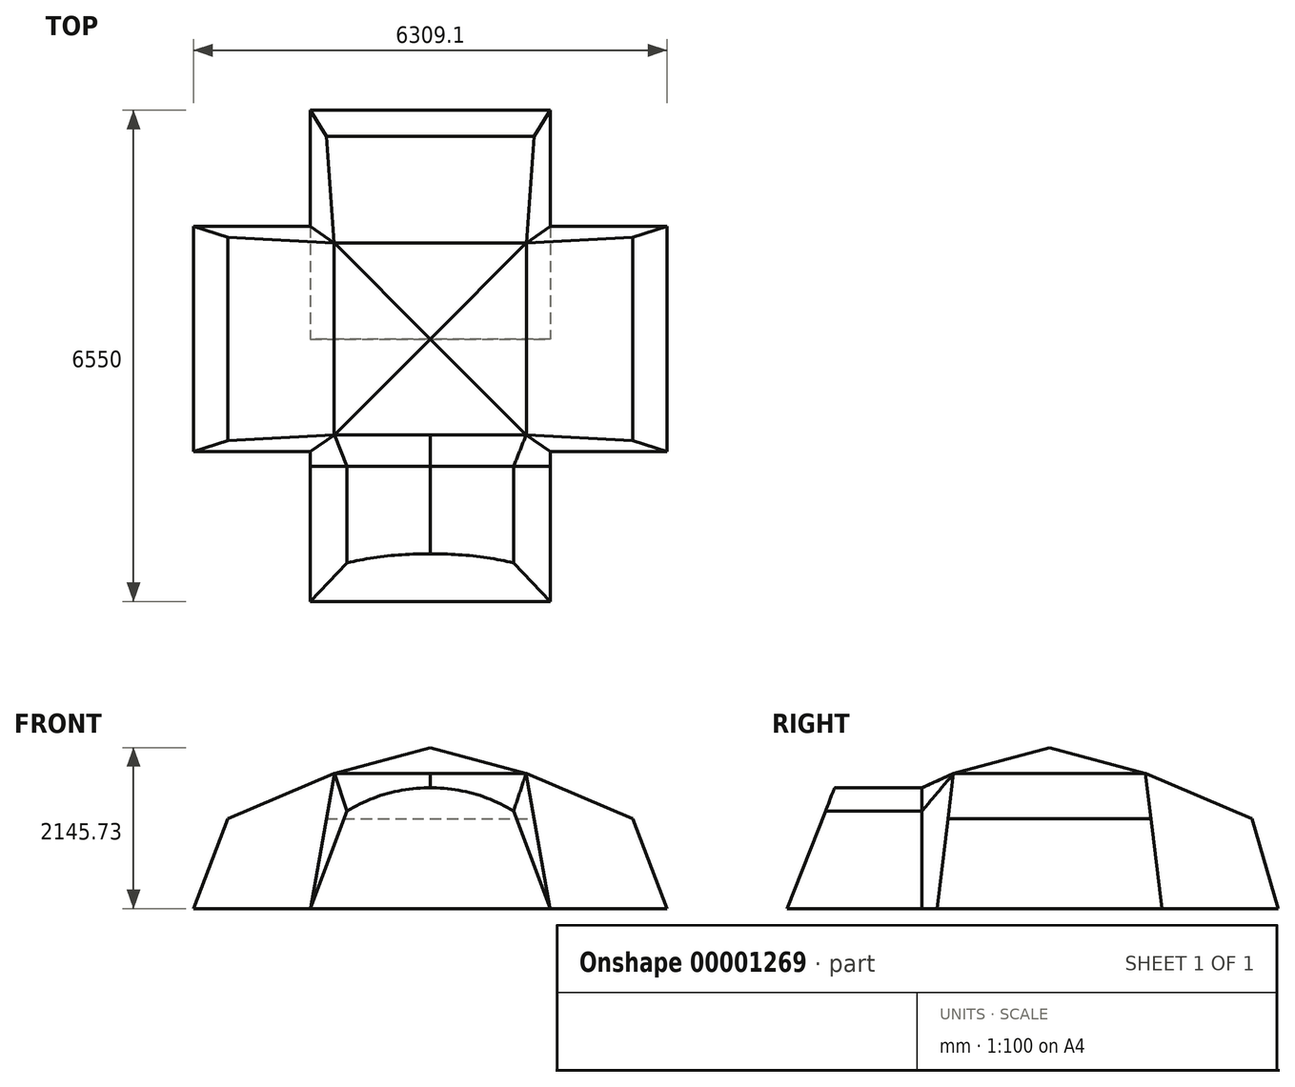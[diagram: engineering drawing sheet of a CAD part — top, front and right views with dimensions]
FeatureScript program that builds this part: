
annotation { "Feature Type Name" : "Feature", "Feature Type Description" : "" }
export const myFeature = defineFeature(function(context is Context, id is Id, definition is map)
    precondition{}
    {
        {
            var Q0;
            Q0=qCreatedBy(makeId("Top.planeOp"),FACE);
            var sketch = newSketch(context, id + "F0", { "sketchPlane" : qUnion([Q0])});
            skLineSegment(sketch, "E0.rect.bottom", {"start": v(0, -1500) * mm, "end": v(-1600, -1500) * mm, "construction": true});
            skLineSegment(sketch, "E0.rect.top", {"start": v(0, 1500) * mm, "end": v(-1600, 1500) * mm, "construction": true});
            skLineSegment(sketch, "E0.rect.right", {"start": v(-1600, -1500) * mm, "end": v(-1600, 1500) * mm, "construction": true});
            skPoint(sketch, "E0.rect.middle", {"position": v(0, 0) * mm});
            skLineSegment(sketch, "E1.bottom", {"start": v(-1600, -1500) * mm, "end": v(-3150, -1500) * mm});
            skLineSegment(sketch, "E1.top", {"start": v(-1600, 1500) * mm, "end": v(-3150, 1500) * mm});
            skLineSegment(sketch, "E1.right", {"start": v(-3150, -1500) * mm, "end": v(-3150, 1500) * mm});
            skLineSegment(sketch, "E2.top", {"start": v(-1600, -3500) * mm, "end": v(0, -3500) * mm});
            skLineSegment(sketch, "E2.left", {"start": v(-1600, -1500) * mm, "end": v(-1600, -3500) * mm});
            skLineSegment(sketch, "E3.top", {"start": v(0, 3050) * mm, "end": v(-1600, 3050) * mm});
            skLineSegment(sketch, "E3.right", {"start": v(-1600, 1500) * mm, "end": v(-1600, 3050) * mm});
            skLineSegment(sketch, "E4", {"start": v(0, 3050) * mm, "end": v(0, -3500) * mm});
            skLineSegment(sketch, "E5", {"start": v(0, 0) * mm, "end": v(-3150, 0) * mm, "construction": true});
            skSolve(sketch);
        }
        {
            var Q0;
            Q0=qCreatedBy(makeId("Front.planeOp"),FACE);
            var sketch = newSketch(context, id + "F1", { "sketchPlane" : qUnion([Q0])});
            skArc(sketch, "E6", {"start": v(0, 1610) * mm, "mid": v(-576.9, 1533.43) * mm, "end": v(-1110, 1300) * mm});
            skPoint(sketch, "E7.rect.middle", {"position": v(0, 0) * mm});
            skLineSegment(sketch, "E8", {"start": v(0, 2145.46) * mm, "end": v(0, 0) * mm});
            skLineSegment(sketch, "E9", {"start": v(-1280, 1799.46) * mm, "end": v(0, 2145.46) * mm});
            skLineSegment(sketch, "E10", {"start": v(-1600, -0.27) * mm, "end": v(-1600, 2068.8) * mm, "construction": true});
            skLineSegment(sketch, "E11", {"start": v(-3154.76, -0.54) * mm, "end": v(-2700, 1199.46) * mm});
            skPoint(sketch, "E12", {"position": v(-2700, 1199.46) * mm});
            skLineSegment(sketch, "E13", {"start": v(-1280, 1799.46) * mm, "end": v(-2700, 1199.46) * mm});
            skLineSegment(sketch, "E14", {"start": v(-1600, -0.27) * mm, "end": v(-1280, 1799.46) * mm});
            skLineSegment(sketch, "E15", {"start": v(-1280, 1799.46) * mm, "end": v(0, 1799.46) * mm});
            skLineSegment(sketch, "E16", {"start": v(0, 1799.46) * mm, "end": v(0, 1610) * mm});
            skLineSegment(sketch, "E17", {"start": v(-1600, -0.27) * mm, "end": v(-1110, 1300) * mm});
            skLineSegment(sketch, "E18", {"start": v(-3154.76, -0.54) * mm, "end": v(0, 0) * mm});
            skSolve(sketch);
        }
        {
            var Q0;
            Q0=qCreatedBy(makeId("Right.planeOp"),FACE);
            var sketch = newSketch(context, id + "F2", { "sketchPlane" : qUnion([Q0])});
            skLineSegment(sketch, "E19", {"start": v(-1500, 0) * mm, "end": v(1500, 0) * mm});
            skLineSegment(sketch, "E20", {"start": v(-3500, 0) * mm, "end": v(0, 0) * mm});
            skLineSegment(sketch, "E21", {"start": v(0, 0) * mm, "end": v(0, 1800) * mm});
            skLineSegment(sketch, "E22.MirrorCS", {"start": v(3050, 0) * mm, "end": v(2701.24, 1200) * mm});
            skLineSegment(sketch, "E23.MirrorCS", {"start": v(1280, 1800) * mm, "end": v(2701.24, 1200) * mm});
            skLineSegment(sketch, "E24", {"start": v(1280, 1800) * mm, "end": v(0, 2145.46) * mm});
            skLineSegment(sketch, "E25", {"start": v(1500, 0) * mm, "end": v(3050, 0) * mm});
            skLineSegment(sketch, "E26", {"start": v(1500, 0) * mm, "end": v(1280, 1800) * mm});
            skLineSegment(sketch, "E27", {"start": v(0, 1800) * mm, "end": v(1280, 1800) * mm});
            skLineSegment(sketch, "E28.MirrorCS", {"start": v(0, 1800) * mm, "end": v(-1280, 1800) * mm});
            skLineSegment(sketch, "E29", {"start": v(-1500, 0) * mm, "end": v(-1280, 1800) * mm});
            skLineSegment(sketch, "E30", {"start": v(0, 2145.46) * mm, "end": v(-1280, 1800) * mm});
            skLineSegment(sketch, "E31", {"start": v(1280, 1800) * mm, "end": v(3050, 1800) * mm});
            skLineSegment(sketch, "E32", {"start": v(3050, 0) * mm, "end": v(3050, 1800) * mm});
            skSolve(sketch);
        }
        {
            var Q0;
            {var subQ0=sQuery(id+"F1.wireOp",EDGE,"E9");Q0=makeQuery(id+"F1.imprint","IMPRINT",FACE,{"disambiguationData":[TD([[makeQuery(id+"F1.imprint","IMPRINT",EDGE,{"derivedFrom":subQ0}),-1.0]])]});}
            var Q1;
            {var subQ1=sQuery(id+"F1.wireOp",EDGE,"E6");Q1=makeQuery(id+"F1.imprint","IMPRINT",FACE,{"disambiguationData":[TD([[makeQuery(id+"F1.imprint","IMPRINT",EDGE,{"derivedFrom":subQ1}),-1.0]])]});}
            var Q2;
            {var subQ0=sQuery(id+"F1.wireOp",EDGE,"E6");Q2=makeQuery(id+"F1.imprint","IMPRINT",FACE,{"disambiguationData":[TD([[makeQuery(id+"F1.imprint","IMPRINT",EDGE,{"derivedFrom":subQ0}),1.0]])]});}
            var Q3;
            Q3=makeQuery(id+"F1.imprint","IMPRINT",FACE,{"disambiguationData":[TD([[makeQuery(id+"F1.imprint","IMPRINT",EDGE,{"derivedFrom":sQuery(id+"F1.wireOp",EDGE,"E11")}),-1.0]])]});
            extrude(context, id + "F3", {"entities" : qUnion([Q0, Q1, Q2, Q3]), "depth" : 3000 * mm, "symmetric" : true});
        }
        {
            var Q0;
            Q0=makeQuery(id+"F2.imprint","IMPRINT",FACE,{"disambiguationData":[TD([[makeQuery(id+"F2.imprint","IMPRINT",EDGE,{"derivedFrom":sQuery(id+"F2.wireOp",EDGE,"E19")}),1.0]])]});
            var Q1;
            {var subQ0=sQuery(id+"F2.wireOp",EDGE,"E21");Q1=makeQuery(id+"F2.imprint","IMPRINT",FACE,{"disambiguationData":[TD([[makeQuery(id+"F2.imprint","IMPRINT",EDGE,{"derivedFrom":subQ0}),1.0]])]});}
            var Q2;
            Q2=makeQuery(id+"F2.imprint","IMPRINT",FACE,{"disambiguationData":[TD([[makeQuery(id+"F2.imprint","IMPRINT",EDGE,{"derivedFrom":sQuery(id+"F2.wireOp",EDGE,"E24")}),1.0]])]});
            extrude(context, id + "F4", {"entities" : qUnion([Q0, Q1, Q2]), "endBound" : BoundingType.THROUGH_ALL, "oppositeDirection" : true, "depth" : 25 * mm});
        }
        {
            var Q0;
            Q0=makeQuery(id+"F3.opExtrude","SWEPT_BODY",BODY,{"disambiguationData":[OSD([sQuery(id+"F1.wireOp",EDGE,"Xvd5dFMZ-jNcX-Ucb9-bvO1-MwbrNxKdaCLq"),sQuery(id+"F1.wireOp",EDGE,"E8"),sQuery(id+"F1.wireOp",EDGE,"RLxnpl80-5fBU-0mOa-wwV0-KRWTK9u8bCjc"),sQuery(id+"F1.wireOp",EDGE,"EUPgxmXC-UgH8-68lH-l14z-mJBkiR1HmSiJ"),sQuery(id+"F1.wireOp",EDGE,"hKe99D8e-fNL4-cCRz-ftVi-nbzCdolXdidr"),sQuery(id+"F1.wireOp",EDGE,"E9"),sQuery(id+"F1.wireOp",EDGE,"3PypLJPX-mRjL-52bw-4543-BBKnZF31eR1R")])]});
            var Q1;
            Q1=makeQuery(id+"F4.opExtrude","SWEPT_BODY",BODY,{"disambiguationData":[OSD([sQuery(id+"F2.wireOp",EDGE,"P1kYks3J-w5it-KXc5-R3qa-AJNZSjgz1d9b"),sQuery(id+"F2.wireOp",EDGE,"E19"),sQuery(id+"F2.wireOp",EDGE,"Bey575iA-ra3J-ZuHC-D0n3-nCMI48ZBgRC3"),sQuery(id+"F2.wireOp",EDGE,"HjRwhLMJ-weJm-YmU8-mPxP-ucW0t3Buu9q5")])]});
            booleanBodies(context, id + "F5", {"operationType" : BooleanOperationType.INTERSECTION, "tools" : qUnion([Q0, Q1])});
        }
        {
            var Q0;
            {var subQ0=sQuery(id+"F1.wireOp",EDGE,"E6");Q0=makeQuery(id+"F1.imprint","IMPRINT",FACE,{"disambiguationData":[TD([[makeQuery(id+"F1.imprint","IMPRINT",EDGE,{"derivedFrom":subQ0}),1.0]])]});}
            var Q1;
            Q1=makeQuery(id+"F1.imprint","IMPRINT",FACE,{"disambiguationData":[TD([[makeQuery(id+"F1.imprint","IMPRINT",EDGE,{"derivedFrom":sQuery(id+"F1.wireOp",EDGE,"E6")}),-1.0]])]});
            extrude(context, id + "F6", {"entities" : qUnion([Q0, Q1]), "operationType" : NewBodyOperationType.ADD, "oppositeDirection" : true, "depth" : 3050 * mm});
        }
        {
            var Q0;
            Q0=makeQuery(id+"F2.imprint","IMPRINT",FACE,{"disambiguationData":[TD([[makeQuery(id+"F2.imprint","IMPRINT",EDGE,{"derivedFrom":sQuery(id+"F2.wireOp",EDGE,"E22.MirrorCS")}),-1.0]])]});
            extrude(context, id + "F7", {"entities" : qUnion([Q0]), "oppositeDirection" : true, "depth" : 1600 * mm});
        }
        {
            var Q0;
            Q0=makeQuery(id+"F7.opExtrude","SWEPT_BODY",BODY,{"disambiguationData":[OSD([sQuery(id+"F2.wireOp",EDGE,"E22.MirrorCS"),sQuery(id+"F2.wireOp",EDGE,"E23.MirrorCS"),sQuery(id+"F2.wireOp",EDGE,"E31"),sQuery(id+"F2.wireOp",EDGE,"E32")])]});
            var Q1;
            Q1=makeQuery(id+"F5.opBoolean","INTERSECT",BODY,{"derivedFrom":[makeQuery(id+"F3.opExtrude","SWEPT_BODY",BODY,{"disambiguationData":[OSD([sQuery(id+"F1.wireOp",EDGE,"E8"),sQuery(id+"F1.wireOp",EDGE,"E9"),sQuery(id+"F1.wireOp",EDGE,"E11"),sQuery(id+"F1.wireOp",EDGE,"E13"),sQuery(id+"F1.wireOp",EDGE,"Teodi1go-UYSe-c90d-j5Cj-GVF7i5q4vz0N"),sQuery(id+"F1.wireOp",EDGE,"ibvV4wT8-ciRc-sWCO-W4sT-jfeLRyLxZu63")])]}),makeQuery(id+"F4.opExtrude","SWEPT_BODY",BODY,{"disambiguationData":[OSD([sQuery(id+"F2.wireOp",EDGE,"E19"),sQuery(id+"F2.wireOp",EDGE,"E20"),sQuery(id+"F2.wireOp",EDGE,"E24"),sQuery(id+"F2.wireOp",EDGE,"E26"),sQuery(id+"F2.wireOp",EDGE,"E29"),sQuery(id+"F2.wireOp",EDGE,"E30")])]})]});
            booleanBodies(context, id + "F8", {"operationType" : BooleanOperationType.SUBTRACTION, "tools" : qUnion([Q0]), "targets" : qUnion([Q1])});
        }
        {
            var Q0;
            {var subQ0=sQuery(id+"F1.wireOp",EDGE,"E6");Q0=makeQuery(id+"F1.imprint","IMPRINT",FACE,{"disambiguationData":[TD([[makeQuery(id+"F1.imprint","IMPRINT",EDGE,{"derivedFrom":subQ0}),1.0]])]});}
            cPlane(context, id + "F9", {"entities" : qUnion([Q0]), "cplaneType" : CPlaneType.OFFSET, "offset" : 1700 * mm, "width" : 150 * mm, "height" : 150 * mm});
        }
        {
            var Q0;
            Q0=qCreatedBy(id+"F9.planeOp",FACE);
            var sketch = newSketch(context, id + "F10", { "sketchPlane" : qUnion([Q0])});
            skLineSegment(sketch, "E33.0.0", {"start": v(0, 0) * mm, "end": v(0, 1610) * mm});
            skArc(sketch, "E33.0.1", {"start": v(0, 1610) * mm, "mid": v(-576.9, 1533.43) * mm, "end": v(-1110, 1300) * mm});
            skLineSegment(sketch, "E33.0.2", {"start": v(-1110, 1300) * mm, "end": v(-1600, -0.27) * mm});
            skLineSegment(sketch, "E33.0.3", {"start": v(-1600, -0.27) * mm, "end": v(0, 0) * mm});
            skSolve(sketch);
        }
        {
            var Q0;
            Q0=makeQuery(id+"F4.opExtrude","SWEPT_FACE",FACE,{"disambiguationData":[OSD([sQuery(id+"F2.wireOp",EDGE,"E29")])]});
            var sketch = newSketch(context, id + "F11", { "sketchPlane" : qUnion([Q0])});
            skLineSegment(sketch, "E34", {"start": v(-1278.02, 1631.42) * mm, "end": v(-1598.16, -181.98) * mm});
            skSolve(sketch);
        }
        {
            var Q1;
            {var subQ0=sQuery(id+"F11.wireOp",EDGE,"E34");Q1=makeQuery(id+"F11.imprint","IMPRINT",FACE,{"disambiguationData":[TD([[makeQuery(id+"F11.imprint","IMPRINT",EDGE,{"derivedFrom":subQ0}),1.0]])]});}
            var Q2;
            Q2=makeQuery(id+"F10.imprint","IMPRINT",FACE,{"disambiguationData":[TD([[makeQuery(id+"F10.imprint","IMPRINT",EDGE,{"derivedFrom":sQuery(id+"F10.wireOp",EDGE,"E33.0.0")}),1.0]])]});
            loft(context, id + "F12", {"operationType" : NewBodyOperationType.ADD, "sheetProfilesArray" : [{ "sheetProfileEntities" : qUnion([Q1]) }, { "sheetProfileEntities" : qUnion([Q2]) }]});
        }
        {
            var Q0;
            Q0=makeQuery(id+"F12.opLoft","CAP_FACE",FACE,{"disambiguationData":[OSD([makeQuery(id+"F10.imprint","IMPRINT",FACE,{"disambiguationData":[TD([[makeQuery(id+"F10.imprint","IMPRINT",EDGE,{"derivedFrom":sQuery(id+"F10.wireOp",EDGE,"E33.0.0")}),1.0]])]})])],"isStart":true});
            extrude(context, id + "F13", {"entities" : qUnion([Q0]), "operationType" : NewBodyOperationType.ADD, "depth" : 1800 * mm});
        }
        {
            var Q0;
            {var subQ0=sQuery(id+"F10.wireOp",EDGE,"E33.0.3");var subQ1=sQuery(id+"F10.wireOp",EDGE,"E33.0.1");var subQ2=sQuery(id+"F10.wireOp",EDGE,"E33.0.0");var subQ3=sQuery(id+"F1.wireOp",EDGE,"E16");var subQ4=sQuery(id+"F1.wireOp",EDGE,"E8");Q0=makeQuery(id+"F13.boolean.opBoolean","MERGE",FACE,{"derivedFrom":[makeQuery(id+"F12.boolean.opBoolean","MERGE",FACE,{"derivedFrom":[makeQuery(id+"F6.boolean.opBoolean","MERGE",FACE,{"derivedFrom":[makeQuery(id+"F3.opExtrude","SWEPT_FACE",FACE,{"disambiguationData":[OSD([subQ4,subQ3])]}),makeQuery(id+"F6.opExtrude","SWEPT_FACE",FACE,{"disambiguationData":[OSD([subQ4,subQ3])]})]}),makeQuery(id+"F12.opLoft","SWEPT_FACE",FACE,{"disambiguationData":[OSD([sQuery(id+"F2.wireOp",EDGE,"E20"),sQuery(id+"F2.wireOp",EDGE,"E28.MirrorCS"),sQuery(id+"F2.wireOp",EDGE,"E29"),sQuery(id+"F2.wireOp",EDGE,"E30"),subQ2,subQ1,subQ0])]})]}),makeQuery(id+"F13.opExtrude","SWEPT_FACE",FACE,{"disambiguationData":[OSD([subQ2,subQ1,subQ0])]})]});}
            var sketch = newSketch(context, id + "F14", { "sketchPlane" : qUnion([Q0])});
            skLineSegment(sketch, "E35.0.0", {"start": v(0, 0) * mm, "end": v(3050, 0) * mm});
            skLineSegment(sketch, "E35.0.1", {"start": v(3050, 0) * mm, "end": v(2701.24, 1200) * mm});
            skLineSegment(sketch, "E35.0.2", {"start": v(2701.24, 1200) * mm, "end": v(1281.27, 1799.46) * mm});
            skLineSegment(sketch, "E35.0.3", {"start": v(1281.27, 1799.46) * mm, "end": v(1280.07, 1799.46) * mm});
            skLineSegment(sketch, "E35.0.4", {"start": v(1280.07, 1799.46) * mm, "end": v(1280, 1800) * mm});
            skLineSegment(sketch, "E35.0.5", {"start": v(1280, 1800) * mm, "end": v(0, 2145.46) * mm});
            skLineSegment(sketch, "E35.0.6", {"start": v(0, 2145.46) * mm, "end": v(-1280, 1800) * mm});
            skFitSpline(sketch, "E35.0.7", {"points": [v(-1280, 1800) * mm, v(-1420, 1736.67) * mm, v(-1560, 1673.33) * mm, v(-1700, 1610) * mm]});
            skFitSpline(sketch, "E35.0.10", {"points": [v(-3500, 0) * mm, v(-2900, 0) * mm, v(-2300, 0) * mm, v(-1700, 0) * mm]});
            skFitSpline(sketch, "E35.0.11", {"points": [v(-1700, 0) * mm, v(-1633.33, 0) * mm, v(-1566.67, 0) * mm, v(-1500, 0) * mm]});
            skLineSegment(sketch, "E35.0.12", {"start": v(-1500, 0) * mm, "end": v(0, 0) * mm});
            skLineSegment(sketch, "E36", {"start": v(-3500, 0) * mm, "end": v(-2863.75, 1610) * mm});
            skLineSegment(sketch, "E37", {"start": v(-3500, 0) * mm, "end": v(-3500, 1795.44) * mm});
            skLineSegment(sketch, "E38", {"start": v(-3500, 1795.44) * mm, "end": v(-2863.75, 1795.44) * mm});
            skLineSegment(sketch, "E39", {"start": v(-2863.75, 1795.44) * mm, "end": v(-2863.75, 1610) * mm});
            skLineSegment(sketch, "E40", {"start": v(-2863.75, 1610) * mm, "end": v(-1700, 1610) * mm});
            skSolve(sketch);
        }
        {
            var Q0;
            {var subQ0=sQuery(id+"F14.wireOp",EDGE,"E36");Q0=makeQuery(id+"F14.imprint","IMPRINT",FACE,{"disambiguationData":[TD([[makeQuery(id+"F14.imprint","IMPRINT",EDGE,{"derivedFrom":subQ0}),1.0]])]});}
            var Q1;
            {var subQ3=sQuery(id+"F14.wireOp",EDGE,"E38");Q1=makeQuery(id+"F14.imprint","IMPRINT",FACE,{"disambiguationData":[TD([[makeQuery(id+"F14.imprint","IMPRINT",EDGE,{"derivedFrom":subQ3}),-1.0]])]});}
            extrude(context, id + "F15", {"entities" : qUnion([Q0, Q1]), "oppositeDirection" : true, "depth" : 1600 * mm});
        }
        {
            var Q0;
            Q0=makeQuery(id+"F15.opExtrude","SWEPT_BODY",BODY,{"disambiguationData":[OSD([sQuery(id+"F14.wireOp",EDGE,"E35.0.9"),sQuery(id+"F14.wireOp",EDGE,"E36"),sQuery(id+"F14.wireOp",EDGE,"awppKT7Z-N9bD-c1A8-NdGw-XdaezunKe1XU")])]});
            var Q1;
            Q1=makeQuery(id+"F5.opBoolean","INTERSECT",BODY,{"derivedFrom":[makeQuery(id+"F3.opExtrude","SWEPT_BODY",BODY,{"disambiguationData":[OSD([sQuery(id+"F1.wireOp",EDGE,"E8"),sQuery(id+"F1.wireOp",EDGE,"E9"),sQuery(id+"F1.wireOp",EDGE,"E11"),sQuery(id+"F1.wireOp",EDGE,"E13"),sQuery(id+"F1.wireOp",EDGE,"E16"),sQuery(id+"F1.wireOp",EDGE,"E18")])]}),makeQuery(id+"F4.opExtrude","SWEPT_BODY",BODY,{"disambiguationData":[OSD([sQuery(id+"F2.wireOp",EDGE,"E19"),sQuery(id+"F2.wireOp",EDGE,"E20"),sQuery(id+"F2.wireOp",EDGE,"E24"),sQuery(id+"F2.wireOp",EDGE,"E26"),sQuery(id+"F2.wireOp",EDGE,"E29"),sQuery(id+"F2.wireOp",EDGE,"E30")])]})]});
            booleanBodies(context, id + "F16", {"operationType" : BooleanOperationType.SUBTRACTION, "tools" : qUnion([Q0]), "targets" : qUnion([Q1])});
        }
        {
            var Q0;
            Q0=makeQuery(id+"F5.opBoolean","INTERSECT",BODY,{"derivedFrom":[makeQuery(id+"F3.opExtrude","SWEPT_BODY",BODY,{"disambiguationData":[OSD([sQuery(id+"F1.wireOp",EDGE,"E8"),sQuery(id+"F1.wireOp",EDGE,"E9"),sQuery(id+"F1.wireOp",EDGE,"E11"),sQuery(id+"F1.wireOp",EDGE,"E13"),sQuery(id+"F1.wireOp",EDGE,"E16"),sQuery(id+"F1.wireOp",EDGE,"E18")])]}),makeQuery(id+"F4.opExtrude","SWEPT_BODY",BODY,{"disambiguationData":[OSD([sQuery(id+"F2.wireOp",EDGE,"E19"),sQuery(id+"F2.wireOp",EDGE,"E20"),sQuery(id+"F2.wireOp",EDGE,"E24"),sQuery(id+"F2.wireOp",EDGE,"E26"),sQuery(id+"F2.wireOp",EDGE,"E29"),sQuery(id+"F2.wireOp",EDGE,"E30")])]})]});
            var Q1;
            Q1=qCreatedBy(makeId("Right.planeOp"),FACE);
            mirror(context, id + "F17", {"operationType" : NewBodyOperationType.ADD, "entities" : qUnion([Q0]), "mirrorPlane" : qUnion([Q1])});
        }
    });
